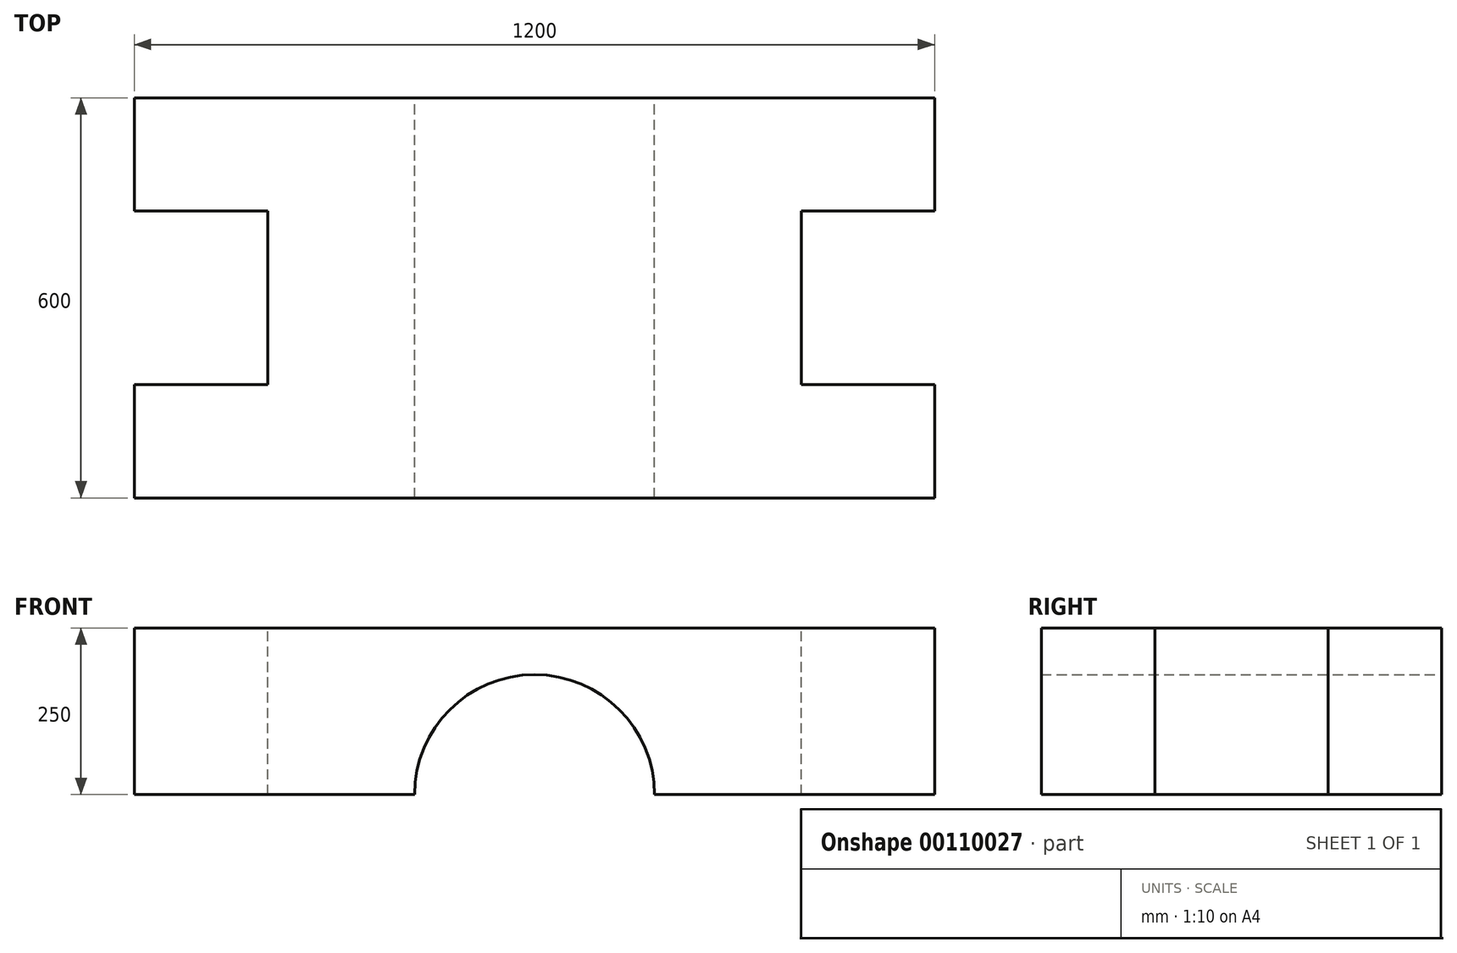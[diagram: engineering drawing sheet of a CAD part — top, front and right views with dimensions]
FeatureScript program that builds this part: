
annotation { "Feature Type Name" : "Feature", "Feature Type Description" : "" }
export const myFeature = defineFeature(function(context is Context, id is Id, definition is map)
    precondition{}
    {
        {
            var Q0;
            Q0=qCreatedBy(makeId("Front.planeOp"),FACE);
            var sketch = newSketch(context, id + "F0", { "sketchPlane" : qUnion([Q0])});
            skLineSegment(sketch, "E0.bottom", {"start": v(-600, 125) * mm, "end": v(600, 125) * mm});
            skLineSegment(sketch, "E0.top", {"start": v(-600, -125) * mm, "end": v(-180, -125) * mm});
            skLineSegment(sketch, "E0.left", {"start": v(-600, 125) * mm, "end": v(-600, -125) * mm});
            skLineSegment(sketch, "E0.right", {"start": v(600, 125) * mm, "end": v(600, -125) * mm});
            skPoint(sketch, "E0.middle", {"position": v(0, 0) * mm});
            skArc(sketch, "E1", {"start": v(180, -125) * mm, "mid": v(0, 55) * mm, "end": v(-180, -125) * mm});
            skLineSegment(sketch, "E2.trimOffspring", {"start": v(180, -125) * mm, "end": v(600, -125) * mm});
            skSolve(sketch);
        }
        {
            var Q0;
            Q0 = qSketchRegion(id + "F0", true);
            extrude(context, id + "F1", {"entities" : qUnion([Q0]), "depth" : 600 * mm});
        }
        {
            var Q0;
            Q0=makeQuery(id+"F1.opExtrude","SWEPT_FACE",FACE,{"disambiguationData":[OSD([sQuery(id+"F0.wireOp",EDGE,"E0.bottom")])]});
            var sketch = newSketch(context, id + "F2", { "sketchPlane" : qUnion([Q0])});
            skLineSegment(sketch, "E3.bottom", {"start": v(-400, -173.46) * mm, "end": v(-600, -173.46) * mm});
            skLineSegment(sketch, "E3.top", {"start": v(-400, -426.54) * mm, "end": v(-600, -426.54) * mm});
            skLineSegment(sketch, "E3.left", {"start": v(-400, -173.46) * mm, "end": v(-400, -426.54) * mm});
            skPoint(sketch, "E3.middle", {"position": v(-600, -300) * mm});
            skLineSegment(sketch, "E4.bottom", {"start": v(400, -430) * mm, "end": v(600, -430) * mm});
            skLineSegment(sketch, "E4.top", {"start": v(400, -170) * mm, "end": v(600, -170) * mm});
            skLineSegment(sketch, "E4.left", {"start": v(400, -430) * mm, "end": v(400, -170) * mm});
            skPoint(sketch, "E4.middle", {"position": v(600, -300) * mm});
            skPoint(sketch, "E5.end.orphan", {"position": v(-800, -173.46) * mm});
            skPoint(sketch, "E6.end.orphan", {"position": v(-800, -426.54) * mm});
            skLineSegment(sketch, "E7", {"start": v(600, -170) * mm, "end": v(600, -430) * mm});
            skPoint(sketch, "E8.start.orphan", {"position": v(800, -170) * mm});
            skPoint(sketch, "E9.end.orphan", {"position": v(800, -430) * mm});
            skSolve(sketch);
        }
        {
            var Q0;
            Q0=makeQuery(id+"F2.imprint","IMPRINT",FACE,{"disambiguationData":[TD([[makeQuery(id+"F2.imprint","IMPRINT",EDGE,{"derivedFrom":sQuery(id+"F2.wireOp",EDGE,"E4.bottom")}),1.0]])]});
            extrude(context, id + "F3", {"entities" : qUnion([Q0]), "operationType" : NewBodyOperationType.REMOVE, "endBound" : BoundingType.THROUGH_ALL, "oppositeDirection" : true, "depth" : 25.4 * mm});
        }
        {
            var Q0;
            Q0=makeQuery(id+"F1.opExtrude","SWEPT_FACE",FACE,{"disambiguationData":[OSD([sQuery(id+"F0.wireOp",EDGE,"E0.bottom")])]});
            var sketch = newSketch(context, id + "F4", { "sketchPlane" : qUnion([Q0])});
            skLineSegment(sketch, "E10.bottom", {"start": v(-600, -170) * mm, "end": v(-400, -170) * mm});
            skLineSegment(sketch, "E10.top", {"start": v(-600, -430) * mm, "end": v(-400, -430) * mm});
            skLineSegment(sketch, "E10.right", {"start": v(-400, -170) * mm, "end": v(-400, -430) * mm});
            skPoint(sketch, "E10.middle", {"position": v(-600, -300) * mm});
            skPoint(sketch, "E11.start.orphan", {"position": v(-600, -170) * mm});
            skPoint(sketch, "E12.end.orphan", {"position": v(-600, -430) * mm});
            skPoint(sketch, "E10.left.end.orphan", {"position": v(-800, -430) * mm});
            skPoint(sketch, "E10.left.start.orphan", {"position": v(-800, -170) * mm});
            skSolve(sketch);
        }
        {
            var Q0;
            Q0 = qSketchRegion(id + "F4", true);
            var Q1;
            {var subQ0=sQuery(id+"F4.wireOp",EDGE,"E10.bottom");Q1=makeQuery(id+"F4.imprint","IMPRINT",FACE,{"disambiguationData":[TD([[makeQuery(id+"F4.imprint","IMPRINT",EDGE,{"derivedFrom":subQ0}),-1.0]])]});}
            extrude(context, id + "F5", {"entities" : qUnion([Q0, Q1]), "operationType" : NewBodyOperationType.REMOVE, "endBound" : BoundingType.THROUGH_ALL, "oppositeDirection" : true, "depth" : 25.4 * mm});
        }
    });
